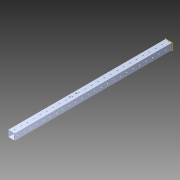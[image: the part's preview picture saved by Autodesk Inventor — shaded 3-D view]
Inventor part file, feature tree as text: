
AUTODESK INVENTOR PART (.ipt)
format: ipt  version: 2014 (Build 180170000, 170)  size: 1,316,864 bytes
history: native  units: in
note: dims shown in document units (in); Inventor stores cm internally (conversion verified against a paired STEP export)
features: extrude x2, sketch x2, pattern_circular x1, other x1, plane x1, imported_body x1, reference x1
ambient origin geometry x8: Origin, YZ Plane, XZ Plane, XY Plane, X Axis, Y Axis, Z Axis, Center Point
bodies: Body1 (feature_tree)
feature tree (9):
  pattern_circular  "CirPattern2"
  other  "217-3426-STEP1"
  plane  "Work Plane1"
  extrude  "Extrusion1"  Depth=3937.0079in TaperAngle=0.0deg
  extrude  "Extrusion7"  [1 undecoded]
  imported_body  "Base1"
  sketch  "Sketch1"  dims[d0=-24.5in d1=3937.0079in d2=0.0in]
  sketch  "Sketch8"  dims[d13=3.937in d14=0.0in]
  reference  "Reference6"
note: 1 required parameter value undecoded (feature->parameter linkage not recoverable at this tier; creation-order binding heuristic only, values carry confidence <= 0.55)
